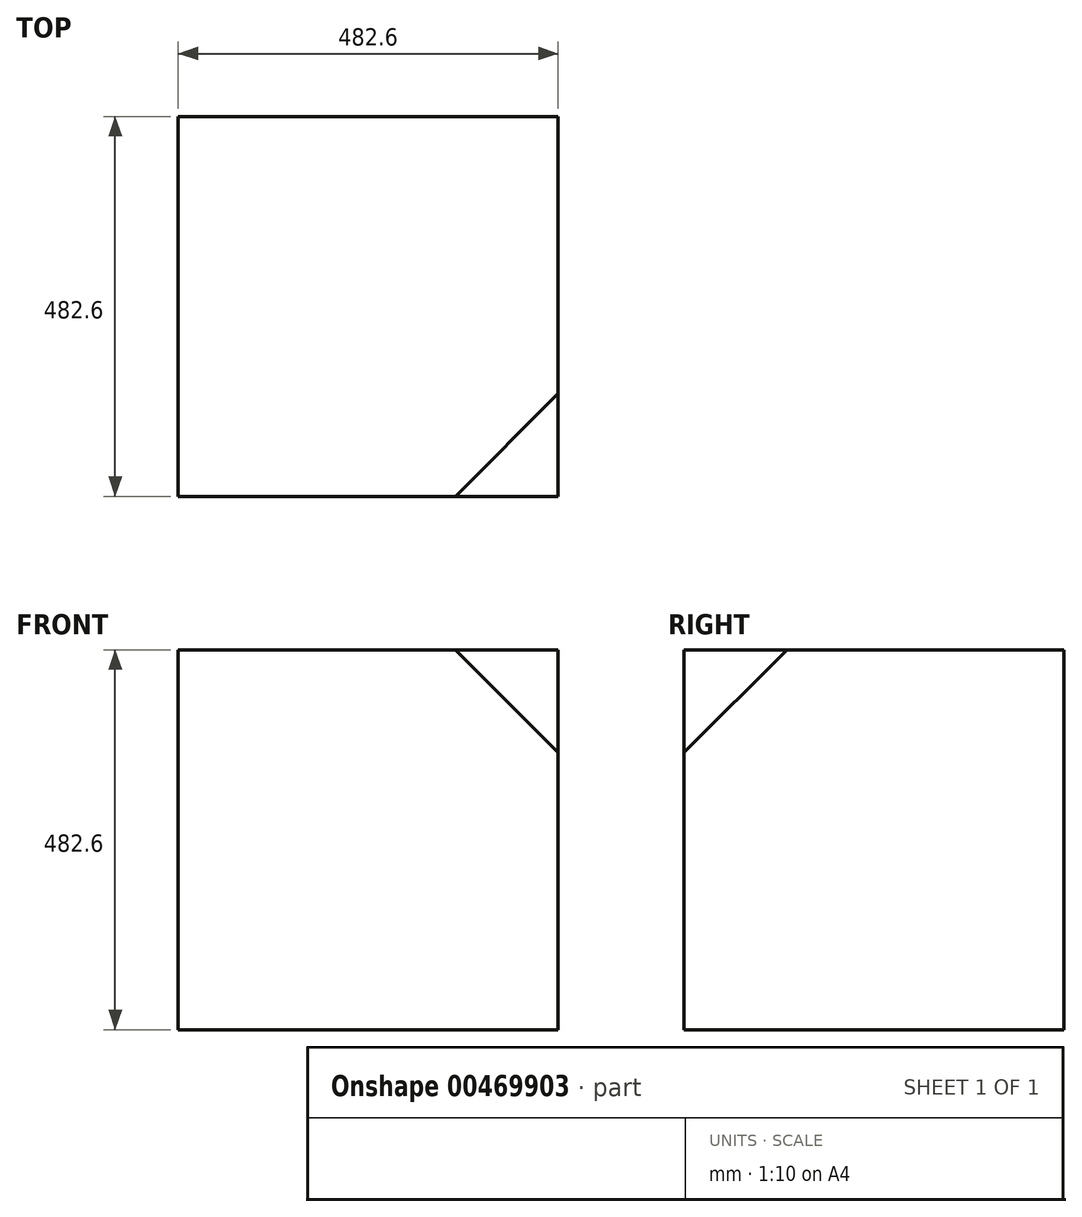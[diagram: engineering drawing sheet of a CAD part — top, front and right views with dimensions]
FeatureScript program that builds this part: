
annotation { "Feature Type Name" : "Feature", "Feature Type Description" : "" }
export const myFeature = defineFeature(function(context is Context, id is Id, definition is map)
    precondition{}
    {
        {
            var Q0;
            Q0=qCreatedBy(makeId("Top.planeOp"),FACE);
            var sketch = newSketch(context, id + "F0", { "sketchPlane" : qUnion([Q0])});
            skLineSegment(sketch, "E0.bottom", {"start": v(241.3, -241.3) * mm, "end": v(-241.3, -241.3) * mm});
            skLineSegment(sketch, "E0.top", {"start": v(241.3, 241.3) * mm, "end": v(-241.3, 241.3) * mm});
            skLineSegment(sketch, "E0.left", {"start": v(241.3, -241.3) * mm, "end": v(241.3, 241.3) * mm});
            skLineSegment(sketch, "E0.right", {"start": v(-241.3, -241.3) * mm, "end": v(-241.3, 241.3) * mm});
            skPoint(sketch, "E0.middle", {"position": v(0, 0) * mm});
            skSolve(sketch);
        }
        {
            var Q0;
            Q0=makeQuery(id+"F0.imprint","IMPRINT",FACE,{"disambiguationData":[TD([[makeQuery(id+"F0.imprint","IMPRINT",EDGE,{"derivedFrom":sQuery(id+"F0.wireOp",EDGE,"E0.bottom")}),-1.0]])]});
            extrude(context, id + "F1", {"entities" : qUnion([Q0]), "endBound" : BoundingType.SYMMETRIC, "depth" : 482.6 * mm});
        }
        {
            var Q0;
            Q0=makeQuery(id+"F1.opExtrude","CAP_VERTEX",VERTEX,{"disambiguationData":[OSD([sQuery(id+"F0.wireOp",EDGE,"E0.bottom"),sQuery(id+"F0.wireOp",EDGE,"E0.right")])],"isStart":false});
            var Q1;
            Q1=makeQuery(id+"F1.opExtrude","CAP_VERTEX",VERTEX,{"disambiguationData":[OSD([sQuery(id+"F0.wireOp",EDGE,"E0.top"),sQuery(id+"F0.wireOp",EDGE,"E0.left")])],"isStart":false});
            var Q2;
            Q2=makeQuery(id+"F1.opExtrude","CAP_VERTEX",VERTEX,{"disambiguationData":[OSD([sQuery(id+"F0.wireOp",EDGE,"E0.bottom"),sQuery(id+"F0.wireOp",EDGE,"E0.left")])],"isStart":true});
            cPlane(context, id + "F2", {"entities" : qUnion([Q0, Q1, Q2]), "cplaneType" : CPlaneType.THREE_POINT, "offset" : 25.4 * mm, "width" : 152.4 * mm, "height" : 152.4 * mm});
        }
        {
            var Q0;
            Q0=qCreatedBy(id+"F2.planeOp",FACE);
            var sketch = newSketch(context, id + "F3", { "sketchPlane" : qUnion([Q0])});
            skCircle(sketch, "E1.cCircle", {"center": v(0, 0) * mm, "radius": 394.04 * mm, "construction": true});
            skLineSegment(sketch, "E1.0", {"start": v(-197.02, 341.25) * mm, "end": v(394.04, 0) * mm});
            skLineSegment(sketch, "E1.1", {"start": v(394.04, 0) * mm, "end": v(-197.02, -341.25) * mm});
            skLineSegment(sketch, "E1.2", {"start": v(-197.02, -341.25) * mm, "end": v(-197.02, 341.25) * mm});
            skSolve(sketch);
        }
        {
            var Q0;
            Q0=makeQuery(id+"F3.imprint","IMPRINT",FACE,{"disambiguationData":[TD([[makeQuery(id+"F3.imprint","IMPRINT",EDGE,{"derivedFrom":sQuery(id+"F3.wireOp",EDGE,"E1.0")}),-1.0]])]});
            extrude(context, id + "F4", {"entities" : qUnion([Q0]), "operationType" : NewBodyOperationType.REMOVE, "depth" : 279.4 * mm, "hasSecondDirection" : true, "secondDirectionOppositeDirection" : false, "secondDirectionDepth" : 203.2 * mm});
        }
    });
